# Revit family: Plumbing_Valves_Leonard-Valve_Nucleus-NV-150-LF-2PS
name_source: partatom
category: Pipe Accessories
revit_build: Autodesk Revit 2018 (Build: 20170223_1515(x64)
units: mm (PartAtom-declared; Revit-internal decimal feet)

## family parameters
Always vertical = Yes
Cut with Voids When Loaded = Yes
OmniClass Number = 23.65.55.14.24
OmniClass Title = Mixing Valves for Liquid Services
Part Type = Normal
Round Connector Dimension = Use Diameter
Shared = No
Work Plane-Based = Yes

## types (1)
- NV-150-LF-2PS
    Assembly Code = D2090800
    Cold Inlet Temperature Range = 39º - 80ºF
    Default Elevation = 48"
    Description = Nucleus-NV-150-LF-2PS
    Edition number = 1
    Hot Inlet Temperature Range = 120º - 180ºF
    Inlet = 2"
    Keynote = 15400
    Manufacturer = Leonard Valve
    Maximum Flow Rate = 330.0 GPM
    Maximum Pressure Drop = 50 psi
    Minimum Flow Rate = 0.3 GPM
    Model = NV 150 LF 2PS
    Offset = 0"
    Outlet = 3"
    Outlet Temperature Range = 65º - 180ºF
    Piping Method = Method W
    Product Guid = 78ca7b4f-ea9f-415e-975f-4cf4455b6664
    Product Material = Bronze - Leonard Valve Company
    Product Page URL = https://www.leonardvalve.com
    Product data url = https://www.bimobject.com
    URL = http://www.leonardvalve.com
    Water Pressure Maximum = 125 psi

## geometry (parser evidence)
native form markers: Sweep x4
no freeform markers — native parametric forms only
